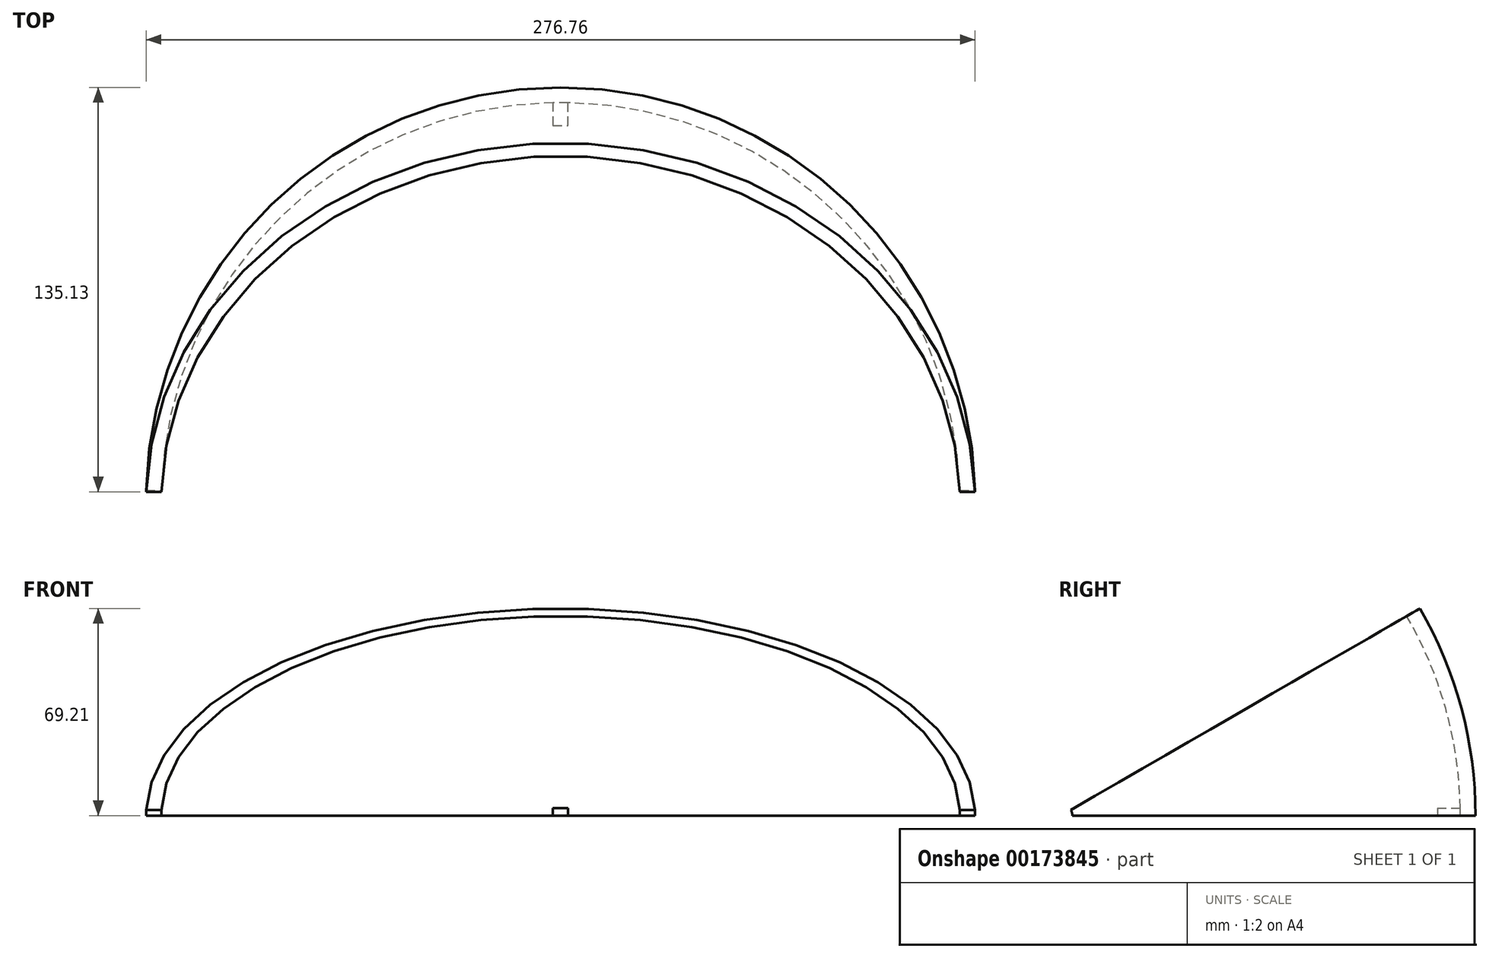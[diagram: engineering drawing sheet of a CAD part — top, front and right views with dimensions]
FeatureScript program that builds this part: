
annotation { "Feature Type Name" : "Feature", "Feature Type Description" : "" }
export const myFeature = defineFeature(function(context is Context, id is Id, definition is map)
    precondition{}
    {
        {
            var Q0;
            Q0=qCreatedBy(makeId("Top.planeOp"),FACE);
            var sketch = newSketch(context, id + "F0", { "sketchPlane" : qUnion([Q0])});
            skLineSegment(sketch, "E0", {"start": v(0, 0) * mm, "end": v(-133.35, 0) * mm, "construction": true});
            skArc(sketch, "E1", {"start": v(-133.35, 0) * mm, "mid": v(0, 133.35) * mm, "end": v(133.35, 0) * mm});
            skLineSegment(sketch, "E2", {"start": v(-133.35, 0) * mm, "end": v(-138.43, 0) * mm});
            skArc(sketch, "E3", {"start": v(-138.43, 0) * mm, "mid": v(0, 138.43) * mm, "end": v(138.43, 0) * mm});
            skLineSegment(sketch, "E4", {"start": v(133.35, 0) * mm, "end": v(138.43, 0) * mm});
            skSolve(sketch);
        }
        {
            var Q0;
            Q0=qSketchRegion(id+"F0",true);
            var Q1;
            Q1=sQuery(id+"F0.wireOp",EDGE,"E0");
            revolve(context, id + "F1", {"entities" : qUnion([Q0]), "axis" : qUnion([Q1]), "revolveType" : RevolveType.ONE_DIRECTION, "oppositeDirection" : true, "angle" : 30 * degree});
        }
        {
            var Q0;
            Q0=qCreatedBy(makeId("Right.planeOp"),FACE);
            var sketch = newSketch(context, id + "F2", { "sketchPlane" : qUnion([Q0])});
            skCircle(sketch, "E5", {"center": v(0, 0) * mm, "radius": 3.81 * mm});
            skSolve(sketch);
        }
        {
            var Q0;
            Q0=qSketchRegion(id+"F2",true);
            extrude(context, id + "F3", {"entities" : qUnion([Q0]), "operationType" : NewBodyOperationType.REMOVE, "endBound" : BoundingType.THROUGH_ALL, "oppositeDirection" : true, "depth" : 25.4 * mm, "hasSecondDirection" : true, "secondDirectionBound" : SecondDirectionBoundingType.THROUGH_ALL, "secondDirectionOppositeDirection" : false, "secondDirectionDepth" : 25.4 * mm});
        }
        {
            var Q0;
            Q0=qCreatedBy(makeId("Top.planeOp"),FACE);
            var sketch = newSketch(context, id + "F4", { "sketchPlane" : qUnion([Q0])});
            skLineSegment(sketch, "E6", {"start": v(0, 0) * mm, "end": v(2.54, 0) * mm, "construction": true});
            skLineSegment(sketch, "E7", {"start": v(0, 0) * mm, "end": v(-2.54, 0) * mm, "construction": true});
            skLineSegment(sketch, "E8", {"start": v(0, 0) * mm, "end": v(-133.35, 0) * mm, "construction": true});
            skLineSegment(sketch, "E9", {"start": v(0, 0) * mm, "end": v(-138.43, 0) * mm, "construction": true});
            skArc(sketch, "E10", {"start": v(-138.43, 0) * mm, "mid": v(0, 138.43) * mm, "end": v(138.43, 0) * mm, "construction": true});
            skArc(sketch, "E11", {"start": v(-133.35, 0) * mm, "mid": v(0, 133.35) * mm, "end": v(133.35, 0) * mm, "construction": true});
            skLineSegment(sketch, "E12", {"start": v(2.54, 0) * mm, "end": v(2.54, 133.33) * mm, "construction": true});
            skArc(sketch, "E13", {"start": v(-2.54, 133.33) * mm, "mid": v(0, 133.35) * mm, "end": v(2.54, 133.33) * mm});
            skLineSegment(sketch, "E14", {"start": v(-2.54, 133.33) * mm, "end": v(-2.54, 125.7) * mm});
            skLineSegment(sketch, "E15", {"start": v(-2.54, 125.7) * mm, "end": v(2.54, 125.7) * mm});
            skLineSegment(sketch, "E16", {"start": v(2.54, 125.7) * mm, "end": v(2.54, 133.33) * mm});
            skSolve(sketch);
        }
        {
            var Q0;
            Q0 = qSketchRegion(id + "F4", true);
            extrude(context, id + "F5", {"entities" : qUnion([Q0]), "operationType" : NewBodyOperationType.ADD, "depth" : 2.54 * mm});
        }
    });
